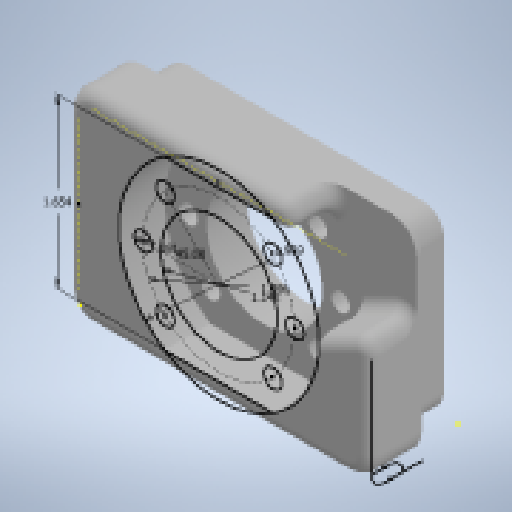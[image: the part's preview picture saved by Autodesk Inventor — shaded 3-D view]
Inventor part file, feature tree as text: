
AUTODESK INVENTOR PART (.ipt)
format: ipt  version: 2023 (Build 270158000, 158)  size: 291,840 bytes
history: native  units: in
note: dims shown in document units (in); Inventor stores cm internally (conversion verified against a paired STEP export)
features: extrude x6, sketch x5, fillet x2
ambient origin geometry x8: Origin, YZ Plane, XZ Plane, XY Plane, X Axis, Y Axis, Z Axis, Center Point
bodies: Solid1 (feature_tree)
feature tree (13):
  extrude  "Extrusion1"  Depth=1.725in
  extrude  "Extrusion2"  Depth=0.3543in TaperAngle=0.0deg
  fillet  "Fillet1"  Radius=3.0in
  sketch  "Sketch3"  dims[d7=2.0in d8=0.25in]
  extrude  "Extrusion3"  Depth=0.25in
  extrude  "Extrusion6"  Depth=0.125in
  extrude  "Extrusion7"  Depth=0.125in
  fillet  "Fillet2"  Radius=0.1811in
  extrude  "Extrusion8"  TaperAngle=45.0deg  [1 undecoded]
  sketch  "Sketch1"  dims[d0=2.725in d1=1.725in]
  sketch  "Sketch2"  dims[d3=0.2in d4=0.3543in d5=0.0in d6=3.0in]
  sketch  "Sketch9"  dims[d9=0.5in d10=0.0in d11=0.125in]
  sketch  "Sketch10"  dims[d12=1.1417in d13=1.4961in d14=0.1811in d15=45.0deg d16=0.5in d17=0.0in d28=1.9685in d29=1.6535in d30=0.4528in d31=0.0in d32=67.5deg d33=0.4724in d35=0.8in d36=1.0in d37=0.0in d38=0.125in d40=1.875in d41=0.0in]
note: 1 required parameter value undecoded (feature->parameter linkage not recoverable at this tier; creation-order binding heuristic only, values carry confidence <= 0.55)
